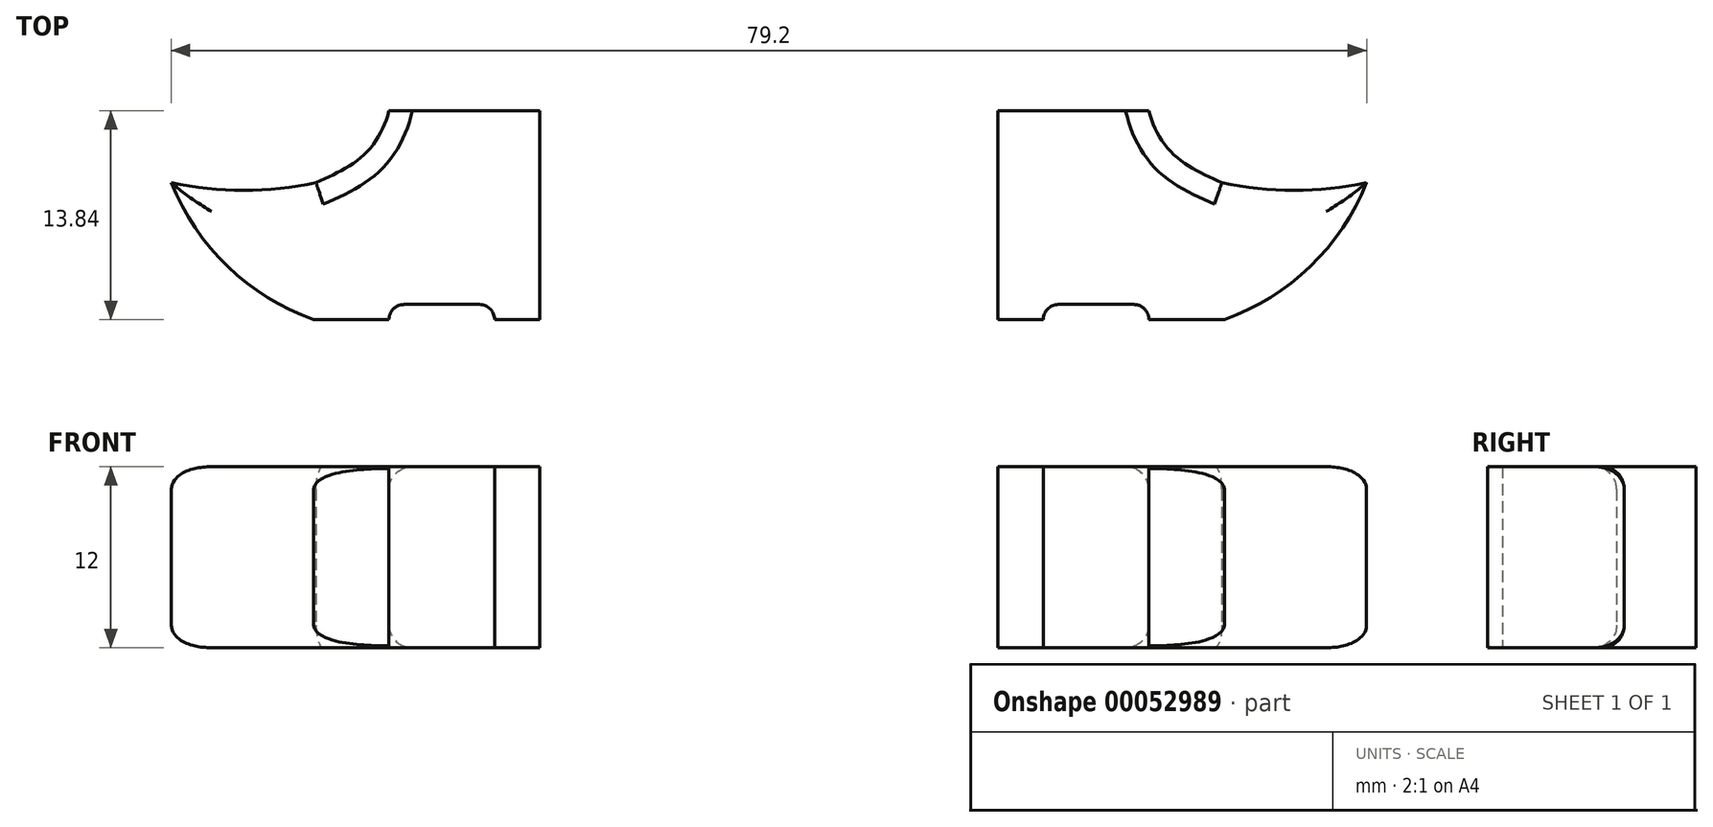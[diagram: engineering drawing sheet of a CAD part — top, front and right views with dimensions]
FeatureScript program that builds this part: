
annotation { "Feature Type Name" : "Feature", "Feature Type Description" : "" }
export const myFeature = defineFeature(function(context is Context, id is Id, definition is map)
    precondition{}
    {
        {
            var Q0;
            Q0=qCreatedBy(makeId("Top.planeOp"),FACE);
            var sketch = newSketch(context, id + "F0", { "sketchPlane" : qUnion([Q0])});
            skArc(sketch, "E0", {"start": v(-39.6, 9.07) * mm, "mid": v(-35.86, 3.52) * mm, "end": v(-30.18, 0) * mm});
            skArc(sketch, "E1", {"start": v(-39.6, 9.07) * mm, "mid": v(-34.8, 8.57) * mm, "end": v(-30, 9.07) * mm});
            skFitSpline(sketch, "E2", {"points": [v(-30, 9.07) * mm, v(-26.72, 11.03) * mm, v(-25.18, 13.84) * mm], "startDerivative": vector(7.02, 3.2) * mm, "endDerivative": vector(1.58, 6.1) * mm});
            skLineSegment(sketch, "E3", {"start": v(-25.18, 13.84) * mm, "end": v(-15.18, 13.84) * mm});
            skLineSegment(sketch, "E4", {"start": v(-15.18, 13.84) * mm, "end": v(-15.18, 0) * mm});
            skLineSegment(sketch, "E5.top", {"start": v(-19.18, 1) * mm, "end": v(-24.18, 1) * mm});
            skArc(sketch, "E6", {"start": v(-18.18, 0) * mm, "mid": v(-18.47, 0.7) * mm, "end": v(-19.18, 1) * mm});
            skArc(sketch, "E7", {"start": v(-24.18, 1) * mm, "mid": v(-24.88, 0.7) * mm, "end": v(-25.18, 0) * mm});
            skLineSegment(sketch, "E8", {"start": v(-25.18, 0) * mm, "end": v(-30.18, 0) * mm});
            skLineSegment(sketch, "E9", {"start": v(-15.18, 0) * mm, "end": v(-18.18, 0) * mm});
            skSolve(sketch);
        }
        {
            var Q0;
            Q0 = qSketchRegion(id + "F0", true);
            var Q1;
            Q1 = qSketchRegion(id + "F0", true);
            extrude(context, id + "F1", {"entities" : qUnion([Q0, Q1]), "depth" : 6 * mm});
        }
        {
            var Q0;
            Q0=makeQuery(id+"F1.opExtrude","CAP_EDGE",EDGE,{"disambiguationData":[OSD([sQuery(id+"F0.wireOp",EDGE,"E1")])],"isStart":false});
            var Q1;
            Q1=makeQuery(id+"F1.opExtrude","CAP_EDGE",EDGE,{"disambiguationData":[OSD([sQuery(id+"F0.wireOp",EDGE,"E0")])],"isStart":false});
            var Q2;
            Q2=makeQuery(id+"F1.opExtrude","CAP_EDGE",EDGE,{"disambiguationData":[OSD([sQuery(id+"F0.wireOp",EDGE,"E2")])],"isStart":false});
            fillet(context, id + "F2", {"entities" : qUnion([Q0, Q1, Q2]), "radius" : 1.5 * mm, "tangentPropagation" : true, "allowEdgeOverflow" : false});
        }
        {
            var Q0;
            Q0=makeQuery(id+"F1.opExtrude","SWEPT_BODY",BODY,{"disambiguationData":[OSD([sQuery(id+"F0.wireOp",EDGE,"r9N5trwQ-pjTS-P4K1-8QWj-axli2bu9RrI8"),sQuery(id+"F0.wireOp",EDGE,"E0"),sQuery(id+"F0.wireOp",EDGE,"E1"),sQuery(id+"F0.wireOp",EDGE,"E2"),sQuery(id+"F0.wireOp",EDGE,"E3"),sQuery(id+"F0.wireOp",EDGE,"E4"),sQuery(id+"F0.wireOp",EDGE,"E5.top"),sQuery(id+"F0.wireOp",EDGE,"9d063ae3-84a6-4d8e-8db5-bfca13e90d22.trimOffspring"),sQuery(id+"F0.wireOp",EDGE,"4a1767ce-735a-453f-8dc4-2587bb333832"),sQuery(id+"F0.wireOp",EDGE,"E6")])]});
            var Q1;
            Q1=qCreatedBy(makeId("Right.planeOp"),FACE);
            mirror(context, id + "F3", {"entities" : qUnion([Q0]), "mirrorPlane" : qUnion([Q1])});
        }
        {
            var Q0;
            Q0=makeQuery(id+"F1.opExtrude","SWEPT_BODY",BODY,{"disambiguationData":[OSD([sQuery(id+"F0.wireOp",EDGE,"E0"),sQuery(id+"F0.wireOp",EDGE,"E1"),sQuery(id+"F0.wireOp",EDGE,"E2"),sQuery(id+"F0.wireOp",EDGE,"E3"),sQuery(id+"F0.wireOp",EDGE,"E4"),sQuery(id+"F0.wireOp",EDGE,"E5.top"),sQuery(id+"F0.wireOp",EDGE,"E6"),sQuery(id+"F0.wireOp",EDGE,"E7"),sQuery(id+"F0.wireOp",EDGE,"E8"),sQuery(id+"F0.wireOp",EDGE,"E9")])]});
            var Q1;
            Q1=makeQuery(id+"F3.opPattern","COPY",BODY,{"derivedFrom":makeQuery(id+"F1.opExtrude","SWEPT_BODY",BODY,{"disambiguationData":[OSD([sQuery(id+"F0.wireOp",EDGE,"E0"),sQuery(id+"F0.wireOp",EDGE,"E1"),sQuery(id+"F0.wireOp",EDGE,"E2"),sQuery(id+"F0.wireOp",EDGE,"E3"),sQuery(id+"F0.wireOp",EDGE,"E4"),sQuery(id+"F0.wireOp",EDGE,"E5.top"),sQuery(id+"F0.wireOp",EDGE,"E6"),sQuery(id+"F0.wireOp",EDGE,"E7"),sQuery(id+"F0.wireOp",EDGE,"E8"),sQuery(id+"F0.wireOp",EDGE,"E9")])]}),"instanceName":"1"});
            var Q2;
            Q2=qCreatedBy(makeId("Top.planeOp"),FACE);
            mirror(context, id + "F4", {"operationType" : NewBodyOperationType.ADD, "entities" : qUnion([Q0, Q1]), "mirrorPlane" : qUnion([Q2])});
        }
    });
